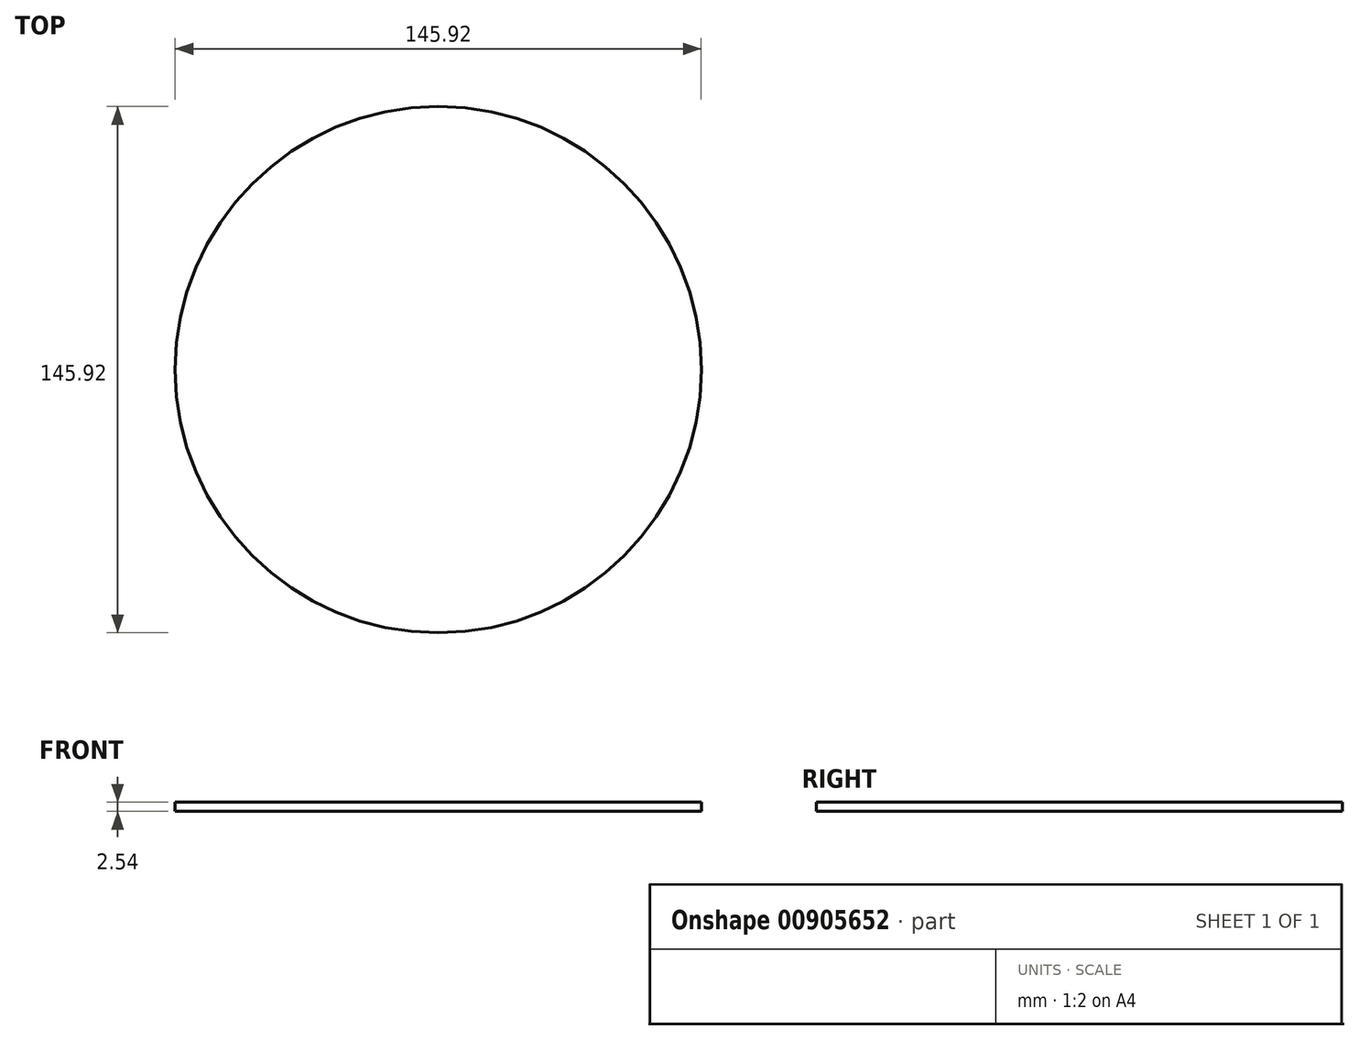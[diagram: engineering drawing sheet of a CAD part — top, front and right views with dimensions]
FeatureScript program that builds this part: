
annotation { "Feature Type Name" : "Feature", "Feature Type Description" : "" }
export const myFeature = defineFeature(function(context is Context, id is Id, definition is map)
    precondition{}
    {
        {
            var Q0;
            Q0=qCreatedBy(makeId("Top.planeOp"),FACE);
            var sketch = newSketch(context, id + "F0", { "sketchPlane" : qUnion([Q0])});
            skCircle(sketch, "E0", {"center": v(0, 0) * mm, "radius": 72.96 * mm});
            skSolve(sketch);
        }
        {
            var Q0;
            Q0 = qSketchRegion(id + "F0", true);
            extrude(context, id + "F1", {"entities" : qUnion([Q0]), "depth" : 2.54 * mm, "offsetDistance" : 25.4 * mm});
        }
        {
            var Q0;
            Q0=qCreatedBy(makeId("Top.planeOp"),FACE);
            var sketch = newSketch(context, id + "F2", { "sketchPlane" : qUnion([Q0])});
            skLineSegment(sketch, "E1.bottom", {"start": v(0, 19.27) * mm, "end": v(1.41, 19.27) * mm});
            skLineSegment(sketch, "E1.top", {"start": v(0, 70.7) * mm, "end": v(1.41, 70.7) * mm});
            skLineSegment(sketch, "E1.left", {"start": v(0, 19.27) * mm, "end": v(0, 70.7) * mm});
            skLineSegment(sketch, "E1.right", {"start": v(1.41, 19.27) * mm, "end": v(1.41, 70.7) * mm});
            skSolve(sketch);
        }
        {
            var Q0;
            Q0=sQuery(id+"F2.wireOp",EDGE,"E1.top");
            var Q1;
            Q1=sQuery(id+"F2.wireOp",EDGE,"E1.bottom");
            var Q2;
            Q2=sQuery(id+"F2.wireOp",EDGE,"E1.left");
            var Q3;
            Q3=sQuery(id+"F2.wireOp",EDGE,"E1.right");
            extrude(context, id + "F3", {"bodyType" : ToolBodyType.SURFACE, "surfaceEntities" : qUnion([Q0, Q1, Q2, Q3]), "depth" : 7.62 * mm, "offsetDistance" : 25.4 * mm});
        }
    });
